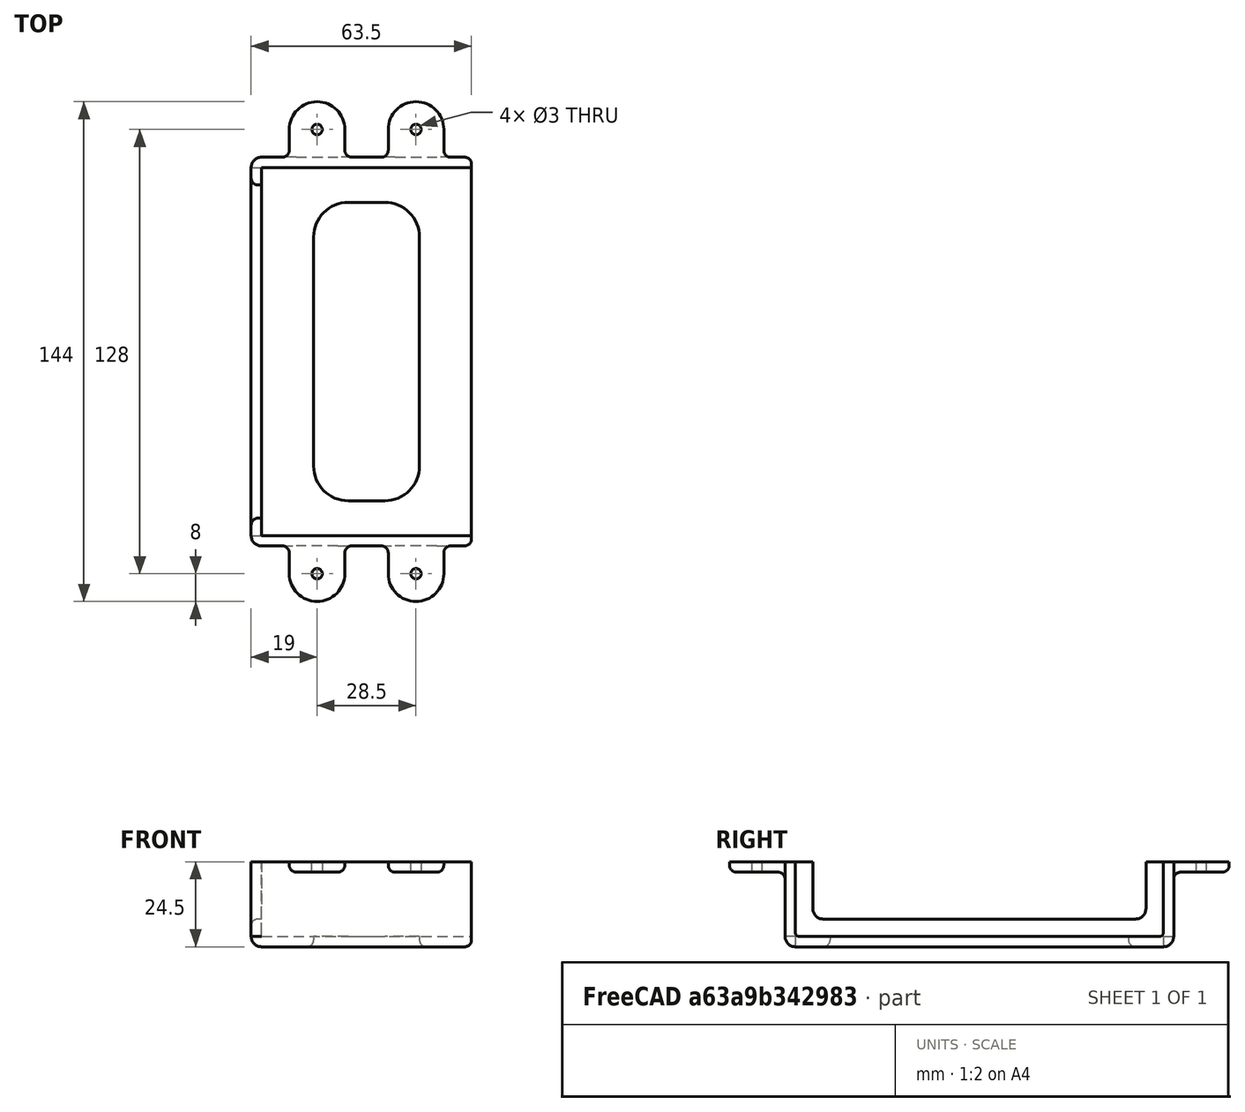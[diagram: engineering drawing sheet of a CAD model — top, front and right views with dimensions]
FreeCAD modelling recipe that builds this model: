
FCSTD DOCUMENT  (FreeCAD 0.21R33668 +7 (Git))
Label: UnderTableBracket-2
License: All rights reserved
LicenseURL: http://en.wikipedia.org/wiki/All_rights_reserved
objects: Sketcher::SketchObject×3, PartDesign::Pocket×2, PartDesign::Fillet×2, Spreadsheet::Sheet×1, PartDesign::AdditiveBox×1, PartDesign::Thickness×1, PartDesign::Pad×1, PartDesign::LinearPattern×1, PartDesign::Plane×1, PartDesign::Mirrored×1, PartDesign::MultiTransform×1, PartDesign::Body×1, App::Part×1, Mesh::Feature×1
note: 22 computed .brp shape members not serialized (recipe doc carries the construction recipe); baked Part::Feature solids carry a one-line shape summary decoded from their .brp

FEATURE [Spreadsheet::Sheet] Spreadsheet
  cells = A1='Width; B1(Width)=106; A2='Height; B2(Height)=21.5; A3='Depth; B3(Depth)=60.5; A4='Screw Diameter; B4(ScrewDiameter)=3
FEATURE [PartDesign::AdditiveBox] Box
  AttacherType = Attacher::AttachEngine3D
  Height = 21.5
  Length = 60.5
  Width = 106
  expr: Height = Spreadsheet.Height
  expr: Length = Spreadsheet.Depth
  expr: Width = Spreadsheet.Width
FEATURE [PartDesign::Thickness] Thickness
  Base = -> Box [Face6,Face2]
  BaseFeature = -> Box
  Intersection = false
  Join = 0
  Mode = 0
  SupportTransform = false
  Value = 3
FEATURE [Sketcher::SketchObject] Sketch
  ExternalGeometry = -> [Thickness]
  FullyConstrained = false
  MapMode = 5
  Placement = pos=(0,0,0) rot=(0.57735,0.57735,0.57735;2.0944rad)
  Support = -> [Thickness]
  sketch-geometry (8):
    g0: LineSegment StartX=101 StartY=21.5 StartZ=0 EndX=101 EndY=8 EndZ=0
    g1: ArcOfCircle CenterX=98 CenterY=8 CenterZ=0 NormalX=0 NormalY=0 NormalZ=1 AngleXU=0 Radius=3 StartAngle=4.71239 EndAngle=6.28319
    g2: LineSegment StartX=98 StartY=5 StartZ=0 EndX=8 EndY=5 EndZ=0
    g3: ArcOfCircle CenterX=8 CenterY=8 CenterZ=0 NormalX=0 NormalY=0 NormalZ=1 AngleXU=0 Radius=3 StartAngle=3.14159 EndAngle=4.71239
    g4: LineSegment StartX=5 StartY=8 StartZ=0 EndX=5 EndY=21.5 EndZ=0
    g5: GeomPoint X=5 Y=35.516 Z=0
    g6: GeomPoint X=101 Y=5 Z=0
    g7: LineSegment StartX=5 StartY=21.5 StartZ=0 EndX=101 EndY=21.5 EndZ=0
  constraints (19):
    c: Tangent(g0,g1) = 1.5708
    c: Tangent(g1,g2) = 1.5708
    c: Tangent(g2,g3) = 1.5708
    c: Tangent(g3,g4) = 1.5708
    c: Horizontal(g2)
    c: Vertical(g0)
    c: Vertical(g4)
    c: Equal(g1,g3)
    c: PointOnObject(g5,g4)
    c: PointOnObject(g6,g0)
    c: PointOnObject(g6,g2)
    c: PointOnObject(g4,g-3)
    c: PointOnObject(g0,g-3)
    c: Radius(g3) = 3
    c: DistanceX(g-3,g4) = 5
    c: DistanceX(g0,g-3) = 5
    c: DistanceY(g-1,g2) = 5
    c: Coincident(g7,g4)
    c: Coincident(g7,g0)
FEATURE [PartDesign::Pocket] Pocket
  BaseFeature = -> Thickness
  Direction = (-1,0,0)
  Length = 5
  Length2 = 5
  Profile = -> Sketch
  ReferenceAxis = -> Sketch [N_Axis]
  Type = 1
FEATURE [Sketcher::SketchObject] Sketch001
  ExternalGeometry = -> [Pocket]
  FullyConstrained = true
  MapMode = 5
  Support = -> [Pocket]
  sketch-geometry (10):
    g0: ArcOfCircle CenterX=25 CenterY=86 CenterZ=0 NormalX=0 NormalY=0 NormalZ=1 AngleXU=0 Radius=10 StartAngle=1.5708 EndAngle=3.14159
    g1: LineSegment StartX=25 StartY=96 StartZ=0 EndX=35.5 EndY=96 EndZ=0
    g2: ArcOfCircle CenterX=35.5 CenterY=86 CenterZ=0 NormalX=0 NormalY=0 NormalZ=1 AngleXU=0 Radius=10 StartAngle=-3.668e-13 EndAngle=1.5708
    g3: LineSegment StartX=45.5 StartY=86 StartZ=0 EndX=45.5 EndY=20 EndZ=0
    g4: ArcOfCircle CenterX=35.5 CenterY=20 CenterZ=0 NormalX=0 NormalY=0 NormalZ=1 AngleXU=0 Radius=10 StartAngle=4.71239 EndAngle=6.28319
    g5: LineSegment StartX=35.5 StartY=10 StartZ=0 EndX=25 EndY=10 EndZ=0
    g6: ArcOfCircle CenterX=25 CenterY=20 CenterZ=0 NormalX=0 NormalY=0 NormalZ=1 AngleXU=0 Radius=10 StartAngle=3.14159 EndAngle=4.71239
    g7: LineSegment StartX=15 StartY=20 StartZ=0 EndX=15 EndY=86 EndZ=0
    g8: GeomPoint X=15 Y=96 Z=0
    g9: GeomPoint X=45.5 Y=10 Z=0
  constraints (24):
    c: Tangent(g0,g1) = 1.5708
    c: Tangent(g1,g2) = 1.5708
    c: Tangent(g2,g3) = 1.5708
    c: Tangent(g3,g4) = 1.5708
    c: Tangent(g4,g5) = 1.5708
    c: Tangent(g5,g6) = 1.5708
    c: Tangent(g6,g7) = 1.5708
    c: Tangent(g7,g0) = 1.5708
    c: Horizontal(g1)
    c: Horizontal(g5)
    c: Vertical(g3)
    c: Vertical(g7)
    c: Equal(g0,g2)
    c: Equal(g2,g4)
    c: Equal(g4,g6)
    c: PointOnObject(g8,g1)
    c: PointOnObject(g8,g7)
    c: PointOnObject(g9,g3)
    c: PointOnObject(g9,g5)
    c: Radius(g2) = 10
    c: DistanceY(g1,g-4) = 10
    c: DistanceY(g-4,g4) = 10
    c: DistanceX(g3,g-4) = 15
    c: DistanceX(g-3,g0) = 15
FEATURE [PartDesign::Pocket] Pocket001
  BaseFeature = -> Pocket
  Direction = (0,0,-1)
  Length = 5
  Length2 = 5
  Profile = -> Sketch001
  ReferenceAxis = -> Sketch001 [N_Axis]
  Type = 1
FEATURE [PartDesign::Fillet] Fillet
  Base = -> Pocket001 [Edge32,Edge34]
  BaseFeature = -> Pocket001
  Radius = 1
  SupportTransform = false
  UseAllEdges = false
FEATURE [Sketcher::SketchObject] Sketch002
  ExternalGeometry = -> [Box]
  FullyConstrained = true
  MapMode = 5
  Placement = pos=(0,0,21.5) rot=(0,0,1;0rad)
  Support = -> [Box]
  expr: Constraints[10] = Spreadsheet.ScrewDiameter
  sketch-geometry (5):
    g0: ArcOfCircle CenterX=16 CenterY=117 CenterZ=0 NormalX=0 NormalY=0 NormalZ=1 AngleXU=0 Radius=8 StartAngle=6e-16 EndAngle=3.14159
    g1: LineSegment StartX=8 StartY=117 StartZ=0 EndX=8 EndY=106 EndZ=0
    g2: LineSegment StartX=24 StartY=106 StartZ=0 EndX=24 EndY=117 EndZ=0
    g3: Circle CenterX=16 CenterY=117 CenterZ=0 NormalX=0 NormalY=0 NormalZ=1 AngleXU=0 Radius=1.5
    g4: LineSegment StartX=8 StartY=106 StartZ=0 EndX=24 EndY=106 EndZ=0
  constraints (13):
    c: Tangent(g0,g1) = -1.5708
    c: Tangent(g2,g0) = -1.5708
    c: Vertical(g1)
    c: PointOnObject(g1,g-3)
    c: PointOnObject(g2,g-3)
    c: Radius(g0) = 8
    c: Vertical(g2)
    c: DistanceY(g2,g2) = 11
    c: DistanceX(g-3,g1) = 8
    c: Coincident(g3,g0)
    c: Diameter(g3) = 3
    c: Coincident(g4,g1)
    c: Coincident(g4,g2)
FEATURE [PartDesign::Pad] Pad
  BaseFeature = -> Fillet
  Direction = (0,0,1)
  Length = 3
  Length2 = 10
  Profile = -> Sketch002
  ReferenceAxis = -> Sketch002 [N_Axis]
  Reversed = true
  Type = 0
FEATURE [PartDesign::LinearPattern] LinearPattern
  Direction = -> Sketch002 [H_Axis]
  Length = 28.5
  Occurrences = 2
  expr: Length = Spreadsheet.Depth - 32
FEATURE [PartDesign::Plane] DatumPlane
  AttachmentOffset = pos=(0,0,0) rot=(-0.57735,0.57735,0.57735;2.0944rad)
  Length = 63.0767
  MapMode = 45
  Placement = pos=(30.25,53,10.75) rot=(-0.57735,0.57735,0.57735;2.0944rad)
  ResizeMode = 0
  Support = -> [Box]
  Width = 98.5767
FEATURE [PartDesign::Mirrored] Mirrored
  MirrorPlane = -> DatumPlane
FEATURE [PartDesign::MultiTransform] MultiTransform
  BaseFeature = -> Pad
  Originals = -> [Pad]
  Transformations = -> [LinearPattern,Mirrored]
FEATURE [PartDesign::Fillet] Fillet001
  Base = -> MultiTransform [Edge42,Edge45,Edge58,Edge73,Edge72,Edge70,Edge69,Edge68,Edge64,Edge66,Edge146,Edge147,Edge145,Edge138,Edge139,Edge137,Edge160,Edge162,Edge161,Edge167,Edge169,Edge168,Edge105,Edge104,Edge101,Edge100,Edge97,Edge95,Edge109,Edge108,Edge87,Edge88,Edge90,Edge91,Edge89,Edge92,Edge124,Edge123,Edge121,Edge120,+2 more]
  BaseFeature = -> MultiTransform
  Radius = 2
  SupportTransform = false
  UseAllEdges = false
FEATURE [PartDesign::Body] Body
  Group = -> [Box,Thickness,Sketch,Pocket,Sketch001,Pocket001,Fillet,Sketch002,Pad,MultiTransform,LinearPattern,DatumPlane,Mirrored,Fillet001]
  Origin = -> Origin001
  Tip = -> Fillet001
FEATURE [App::Part] Part  label="Bracket"
  Group = -> [Body]
  Origin = -> Origin
FEATURE [Mesh::Feature] Mesh  label="Bracket (Meshed)"
